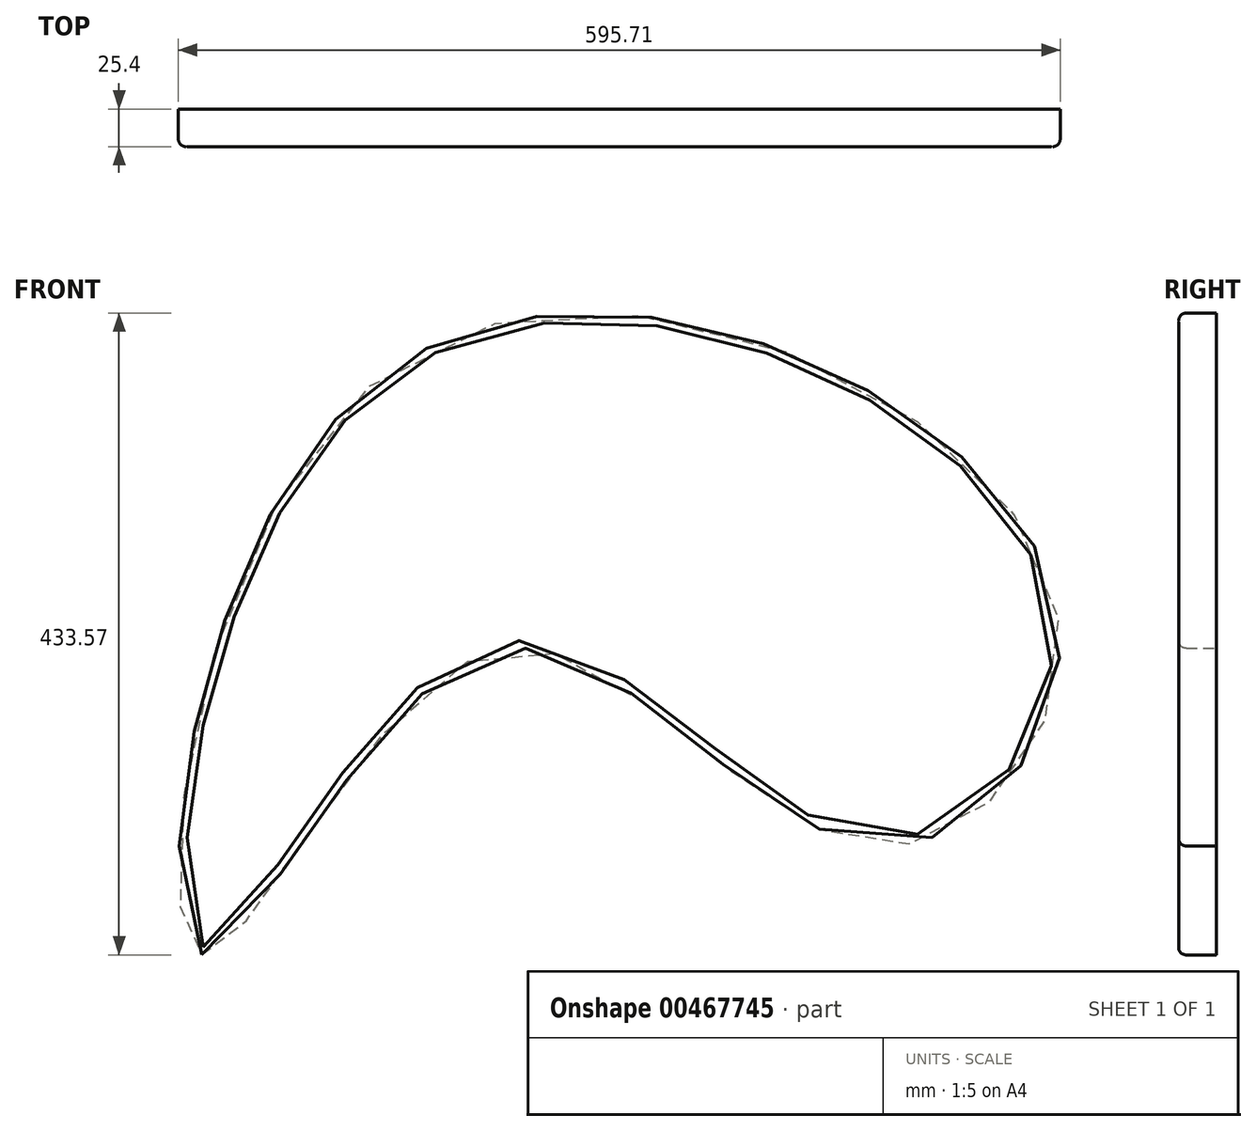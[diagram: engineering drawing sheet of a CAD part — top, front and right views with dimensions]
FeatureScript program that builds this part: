
annotation { "Feature Type Name" : "Feature", "Feature Type Description" : "" }
export const myFeature = defineFeature(function(context is Context, id is Id, definition is map)
    precondition{}
    {
        {
            var Q0;
            Q0=qCreatedBy(makeId("Front.planeOp"),FACE);
            var sketch = newSketch(context, id + "F0", { "sketchPlane" : qUnion([Q0])});
            skFitSpline(sketch, "E0", {"points": [v(-306.58, -93.38) * mm, v(-110.98, 111.24) * mm, v(147.85, -19.59) * mm, v(267.32, 156.03) * mm, v(-180.81, 300.47) * mm, v(-306.58, -93.38) * mm]});
            skSolve(sketch);
        }
        {
            var Q0;
            Q0=makeQuery(id+"F0.imprint","IMPRINT",FACE,{"disambiguationData":[TD([[makeQuery(id+"F0.imprint","IMPRINT",EDGE,{"derivedFrom":sQuery(id+"F0.wireOp",EDGE,"E0")}),1.0]])]});
            extrude(context, id + "F1", {"entities" : qUnion([Q0]), "depth" : 25.4 * mm});
        }
        {
            var Q0;
            Q0=makeQuery(id+"F1.opExtrude","CAP_EDGE",EDGE,{"disambiguationData":[OSD([sQuery(id+"F0.wireOp",EDGE,"E0")])],"isStart":false});
            fillet(context, id + "F2", {"entities" : qUnion([Q0]), "radius" : 5.08 * mm, "tangentPropagation" : true, "allowEdgeOverflow" : false});
        }
    });
